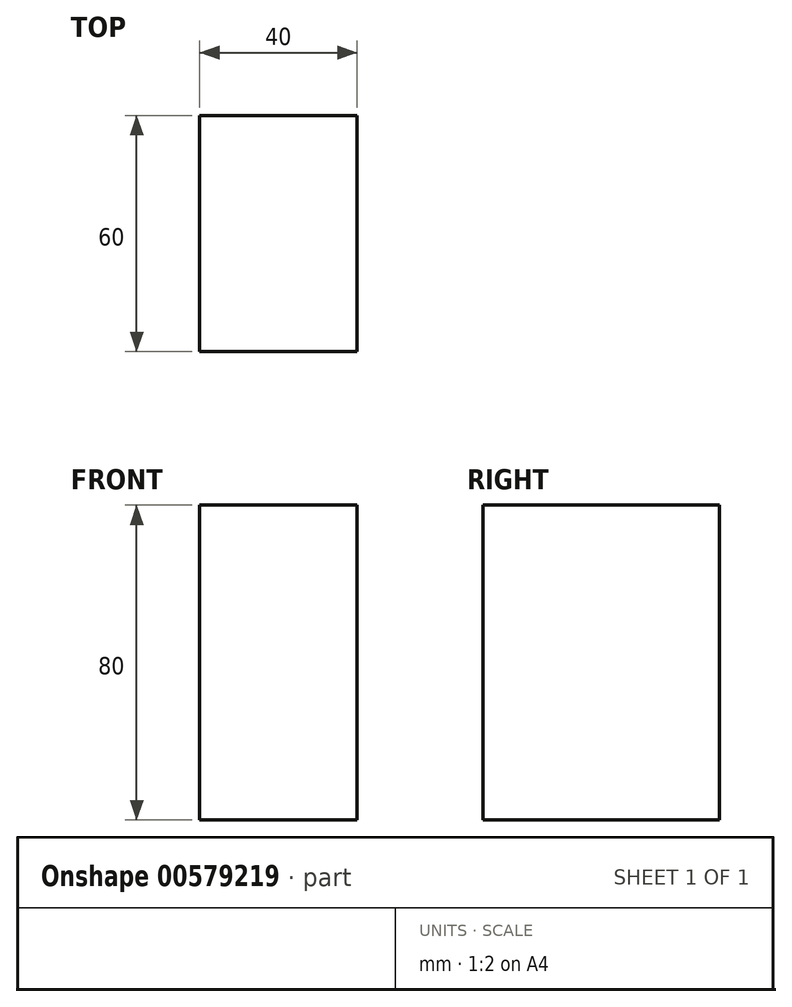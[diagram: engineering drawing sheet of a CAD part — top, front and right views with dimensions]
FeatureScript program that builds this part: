
annotation { "Feature Type Name" : "Feature", "Feature Type Description" : "" }
export const myFeature = defineFeature(function(context is Context, id is Id, definition is map)
    precondition{}
    {
        {
            var Q0;
            Q0=qCreatedBy(makeId("Top.planeOp"),FACE);
            var sketch = newSketch(context, id + "F0", { "sketchPlane" : qUnion([Q0])});
            skLineSegment(sketch, "E0.bottom", {"start": v(0, 42.16) * mm, "end": v(40, 42.16) * mm});
            skLineSegment(sketch, "E0.top", {"start": v(0, -17.84) * mm, "end": v(40, -17.84) * mm});
            skLineSegment(sketch, "E0.left", {"start": v(0, 42.16) * mm, "end": v(0, -17.84) * mm});
            skLineSegment(sketch, "E0.right", {"start": v(40, 42.16) * mm, "end": v(40, -17.84) * mm});
            skSolve(sketch);
        }
        {
            var Q0;
            Q0 = qSketchRegion(id + "F0", true);
            extrude(context, id + "F1", {"entities" : qUnion([Q0]), "depth" : 80 * mm, "offsetDistance" : 25 * mm});
        }
    });
